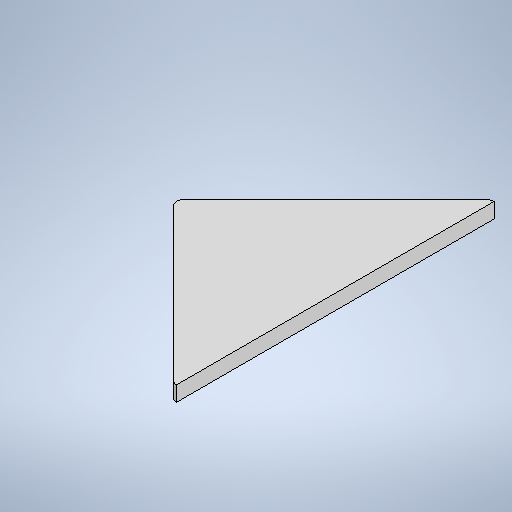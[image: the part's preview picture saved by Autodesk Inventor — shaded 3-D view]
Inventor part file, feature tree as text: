
AUTODESK INVENTOR PART (.ipt)
format: ipt  version: 2025 (Build 290162010, 162A)  size: 262,656 bytes
history: native  units: mm
features: sketch x2, sheet_metal_op x1, chamfer x1, extrude x1, other x1
ambient origin geometry x8: Origin, YZ Plane, XZ Plane, XY Plane, X Axis, Y Axis, Z Axis, Center Point
bodies: Solid1 (feature_tree)
feature tree (6):
  sheet_metal_op  "Face1"
  chamfer  "Corner Round2"
  extrude  "Extrusion1"  Depth=42.0mm
  sketch  "Sketch1"  dims[d0=41.0mm d1=42.0mm]
  other  "Plate1"
  sketch  "Sketch2"  dims[d2=2.0mm d4=62.0mm d6=1.0mm d7=0.0mm d8=0.0mm]
